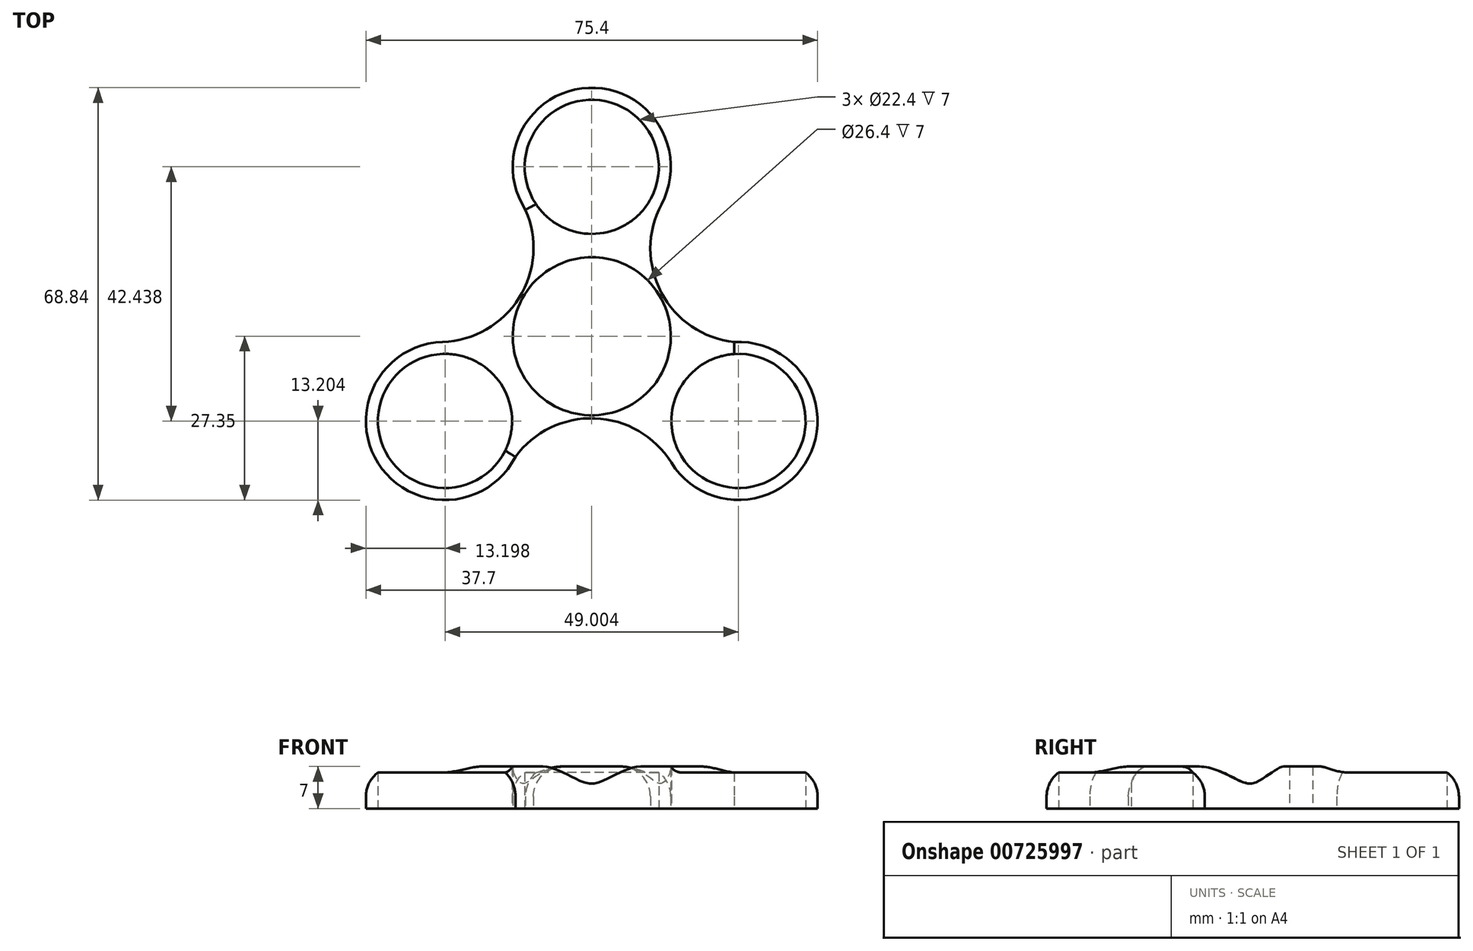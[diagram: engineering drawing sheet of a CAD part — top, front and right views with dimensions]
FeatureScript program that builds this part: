
annotation { "Feature Type Name" : "Feature", "Feature Type Description" : "" }
export const myFeature = defineFeature(function(context is Context, id is Id, definition is map)
    precondition{}
    {
        {
            var Q0;
            Q0=qCreatedBy(makeId("Top.planeOp"),FACE);
            var sketch = newSketch(context, id + "F0", { "sketchPlane" : qUnion([Q0])});
            skCircle(sketch, "E0", {"center": v(0, 0) * mm, "radius": 11.2 * mm});
            skCircle(sketch, "E1", {"center": v(0, 0) * mm, "radius": 13.2 * mm});
            skCircle(sketch, "E2", {"center": v(0, 28.3) * mm, "radius": 11.2 * mm});
            skArc(sketch, "E3", {"start": v(11.63, 22.04) * mm, "mid": v(-0.54, 41.48) * mm, "end": v(-11.07, 21.1) * mm});
            skArc(sketch, "E4.1.0", {"start": v(-24.9, -0.95) * mm, "mid": v(-35.65, -21.21) * mm, "end": v(-12.74, -20.14) * mm});
            skCircle(sketch, "E4.1.1", {"center": v(-24.5, -14.15) * mm, "radius": 11.2 * mm});
            skArc(sketch, "E4.2.0", {"start": v(13.27, -21.09) * mm, "mid": v(36.2, -20.27) * mm, "end": v(23.81, -0.96) * mm});
            skCircle(sketch, "E4.2.1", {"center": v(24.5, -14.15) * mm, "radius": 11.2 * mm});
            skArc(sketch, "E5", {"start": v(11.63, 22.04) * mm, "mid": v(11.61, 7.3) * mm, "end": v(23.81, -0.96) * mm});
            skArc(sketch, "E6.1.0", {"start": v(-24.9, -0.95) * mm, "mid": v(-12.13, 6.4) * mm, "end": v(-11.07, 21.1) * mm});
            skArc(sketch, "E6.2.0", {"start": v(13.27, -21.09) * mm, "mid": v(0.52, -13.7) * mm, "end": v(-12.74, -20.14) * mm});
            skSolve(sketch);
        }
        {
            var Q0;
            Q0=makeQuery(id+"F0.imprint","IMPRINT",FACE,{"disambiguationData":[TD([[makeQuery(id+"F0.imprint","IMPRINT",EDGE,{"derivedFrom":sQuery(id+"F0.wireOp",EDGE,"E1")}),-1.0]])]});
            extrude(context, id + "F1", {"entities" : qUnion([Q0]), "depth" : 7 * mm, "offsetDistance" : 25 * mm});
        }
        {
            var Q0;
            Q0=makeQuery(id+"F1.opExtrude","CAP_EDGE",EDGE,{"disambiguationData":[OSD([sQuery(id+"F0.wireOp",EDGE,"E4.2.0")])],"isStart":false});
            var Q1;
            Q1=makeQuery(id+"F1.opExtrude","CAP_EDGE",EDGE,{"disambiguationData":[OSD([sQuery(id+"F0.wireOp",EDGE,"E4.1.0")])],"isStart":false});
            var Q2;
            Q2=makeQuery(id+"F1.opExtrude","CAP_EDGE",EDGE,{"disambiguationData":[OSD([sQuery(id+"F0.wireOp",EDGE,"E6.2.0")])],"isStart":false});
            var Q3;
            Q3=makeQuery(id+"F1.opExtrude","CAP_EDGE",EDGE,{"disambiguationData":[OSD([sQuery(id+"F0.wireOp",EDGE,"E5")])],"isStart":false});
            var Q4;
            Q4=makeQuery(id+"F1.opExtrude","CAP_EDGE",EDGE,{"disambiguationData":[OSD([sQuery(id+"F0.wireOp",EDGE,"E3")])],"isStart":false});
            var Q5;
            Q5=makeQuery(id+"F1.opExtrude","CAP_EDGE",EDGE,{"disambiguationData":[OSD([sQuery(id+"F0.wireOp",EDGE,"E6.1.0")])],"isStart":false});
            fillet(context, id + "F2", {"entities" : qUnion([Q0, Q1, Q2, Q3, Q4, Q5]), "radius" : 5 * mm, "tangentPropagation" : true, "allowEdgeOverflow" : false});
        }
    });
